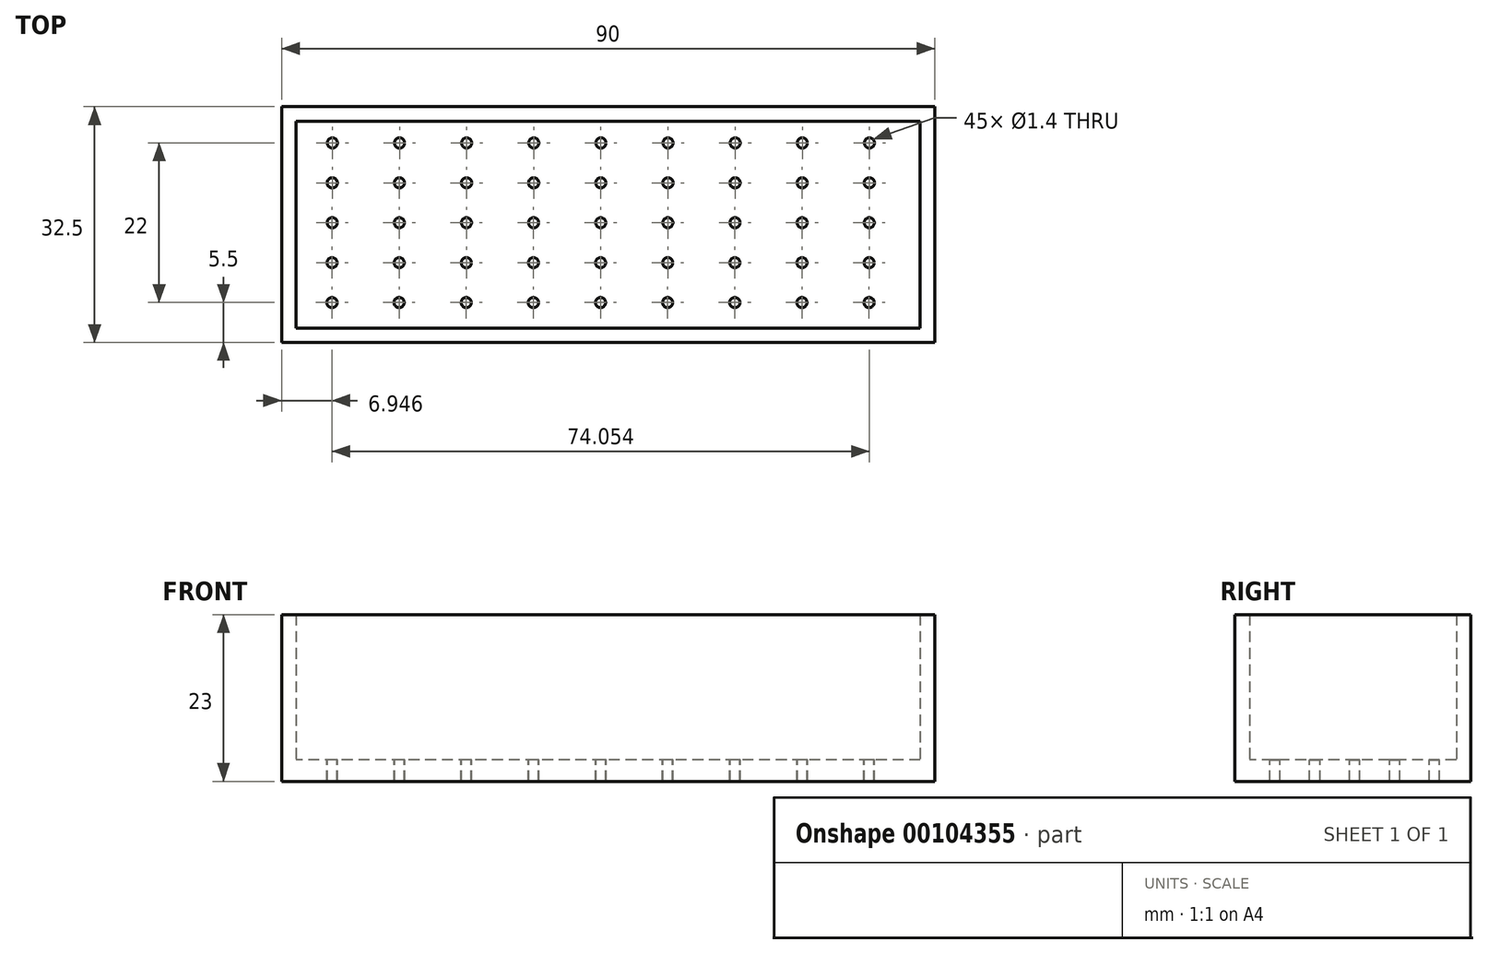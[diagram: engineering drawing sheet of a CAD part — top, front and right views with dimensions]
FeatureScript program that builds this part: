
annotation { "Feature Type Name" : "Feature", "Feature Type Description" : "" }
export const myFeature = defineFeature(function(context is Context, id is Id, definition is map)
    precondition{}
    {
        {
            var Q0;
            Q0=qCreatedBy(makeId("Top.planeOp"),FACE);
            var sketch = newSketch(context, id + "F0", { "sketchPlane" : qUnion([Q0])});
            skLineSegment(sketch, "E0.bottom", {"start": v(-45, 16.25) * mm, "end": v(45, 16.25) * mm});
            skLineSegment(sketch, "E0.top", {"start": v(-45, -16.25) * mm, "end": v(45, -16.25) * mm});
            skLineSegment(sketch, "E0.left", {"start": v(-45, 16.25) * mm, "end": v(-45, -16.25) * mm});
            skLineSegment(sketch, "E0.right", {"start": v(45, 16.25) * mm, "end": v(45, -16.25) * mm});
            skPoint(sketch, "E0.middle", {"position": v(0, 0) * mm});
            skSolve(sketch);
        }
        {
            var Q0;
            Q0 = qSketchRegion(id + "F0", true);
            extrude(context, id + "F1", {"entities" : qUnion([Q0]), "depth" : 3 * mm});
        }
        {
            var Q0;
            Q0=makeQuery(id+"F1.opExtrude","CAP_FACE",FACE,{"disambiguationData":[OSD([sQuery(id+"F0.wireOp",EDGE,"E0.bottom"),sQuery(id+"F0.wireOp",EDGE,"E0.top"),sQuery(id+"F0.wireOp",EDGE,"E0.left"),sQuery(id+"F0.wireOp",EDGE,"E0.right")])],"isStart":false});
            var sketch = newSketch(context, id + "F2", { "sketchPlane" : qUnion([Q0])});
            skLineSegment(sketch, "E1", {"start": v(-45, 16.25) * mm, "end": v(-45, -16.25) * mm});
            skLineSegment(sketch, "E2", {"start": v(-45, -16.25) * mm, "end": v(45, -16.25) * mm});
            skLineSegment(sketch, "E3", {"start": v(45, -16.25) * mm, "end": v(45, 16.25) * mm});
            skLineSegment(sketch, "E4", {"start": v(45, 16.25) * mm, "end": v(-45, 16.25) * mm});
            skLineSegment(sketch, "E5", {"start": v(-43, 14.25) * mm, "end": v(-43, -14.25) * mm});
            skLineSegment(sketch, "E6", {"start": v(-43, -14.25) * mm, "end": v(43, -14.25) * mm});
            skLineSegment(sketch, "E7", {"start": v(43, -14.25) * mm, "end": v(43, 14.25) * mm});
            skLineSegment(sketch, "E8", {"start": v(43, 14.25) * mm, "end": v(-43, 14.25) * mm});
            skSolve(sketch);
        }
        {
            var Q0;
            Q0=makeQuery(id+"F2.imprint","IMPRINT",FACE,{"disambiguationData":[TD([[makeQuery(id+"F2.imprint","IMPRINT",EDGE,{"derivedFrom":sQuery(id+"F2.wireOp",EDGE,"E1")}),1.0]])]});
            extrude(context, id + "F3", {"entities" : qUnion([Q0]), "operationType" : NewBodyOperationType.ADD, "depth" : 20 * mm});
        }
        {
            var Q0;
            Q0=makeQuery(id+"F1.opExtrude","CAP_FACE",FACE,{"disambiguationData":[OSD([sQuery(id+"F0.wireOp",EDGE,"E0.bottom"),sQuery(id+"F0.wireOp",EDGE,"E0.top"),sQuery(id+"F0.wireOp",EDGE,"E0.left"),sQuery(id+"F0.wireOp",EDGE,"E0.right")])],"isStart":false});
            var sketch = newSketch(context, id + "F4", { "sketchPlane" : qUnion([Q0])});
            skCircle(sketch, "E9", {"center": v(-38, 11.25) * mm, "radius": 0.7 * mm});
            skCircle(sketch, "E10.1.0.0", {"center": v(-28.75, 11.25) * mm, "radius": 0.7 * mm});
            skCircle(sketch, "E10.2.0.0", {"center": v(-19.5, 11.25) * mm, "radius": 0.7 * mm});
            skCircle(sketch, "E10.3.0.0", {"center": v(-10.25, 11.25) * mm, "radius": 0.7 * mm});
            skCircle(sketch, "E10.4.0.0", {"center": v(-1, 11.25) * mm, "radius": 0.7 * mm});
            skCircle(sketch, "E10.5.0.0", {"center": v(8.25, 11.25) * mm, "radius": 0.7 * mm});
            skCircle(sketch, "E10.6.0.0", {"center": v(17.5, 11.25) * mm, "radius": 0.7 * mm});
            skCircle(sketch, "E10.7.0.0", {"center": v(26.75, 11.25) * mm, "radius": 0.7 * mm});
            skCircle(sketch, "E10.8.0.0", {"center": v(36, 11.25) * mm, "radius": 0.7 * mm});
            skLineSegment(sketch, "E10.direction1", {"start": v(-38, 11.25) * mm, "end": v(-28.75, 11.25) * mm, "construction": true});
            skCircle(sketch, "E11.1.0.0", {"center": v(-38.01, 5.75) * mm, "radius": 0.7 * mm});
            skCircle(sketch, "E11.2.0.0", {"center": v(-38.03, 0.25) * mm, "radius": 0.7 * mm});
            skCircle(sketch, "E11.3.0.0", {"center": v(-38.04, -5.25) * mm, "radius": 0.7 * mm});
            skCircle(sketch, "E11.4.0.0", {"center": v(-38.05, -10.75) * mm, "radius": 0.7 * mm});
            skLineSegment(sketch, "E11.direction1", {"start": v(-38, 11.25) * mm, "end": v(-38.01, 5.75) * mm, "construction": true});
            skCircle(sketch, "E12.1.0.0", {"center": v(-28.76, 5.75) * mm, "radius": 0.7 * mm});
            skCircle(sketch, "E12.1.0.1", {"center": v(-28.78, 0.25) * mm, "radius": 0.7 * mm});
            skCircle(sketch, "E12.1.0.2", {"center": v(-28.8, -5.25) * mm, "radius": 0.7 * mm});
            skCircle(sketch, "E12.1.0.3", {"center": v(-28.8, -10.75) * mm, "radius": 0.7 * mm});
            skCircle(sketch, "E12.2.0.0", {"center": v(-19.51, 5.75) * mm, "radius": 0.7 * mm});
            skCircle(sketch, "E12.2.0.1", {"center": v(-19.53, 0.25) * mm, "radius": 0.7 * mm});
            skCircle(sketch, "E12.2.0.2", {"center": v(-19.54, -5.25) * mm, "radius": 0.7 * mm});
            skCircle(sketch, "E12.2.0.3", {"center": v(-19.55, -10.75) * mm, "radius": 0.7 * mm});
            skCircle(sketch, "E12.3.0.0", {"center": v(-10.26, 5.75) * mm, "radius": 0.7 * mm});
            skCircle(sketch, "E12.3.0.1", {"center": v(-10.28, 0.25) * mm, "radius": 0.7 * mm});
            skCircle(sketch, "E12.3.0.2", {"center": v(-10.3, -5.25) * mm, "radius": 0.7 * mm});
            skCircle(sketch, "E12.3.0.3", {"center": v(-10.3, -10.75) * mm, "radius": 0.7 * mm});
            skCircle(sketch, "E12.4.0.0", {"center": v(-1.01, 5.75) * mm, "radius": 0.7 * mm});
            skCircle(sketch, "E12.4.0.1", {"center": v(-1.03, 0.25) * mm, "radius": 0.7 * mm});
            skCircle(sketch, "E12.4.0.2", {"center": v(-1.04, -5.25) * mm, "radius": 0.7 * mm});
            skCircle(sketch, "E12.4.0.3", {"center": v(-1.05, -10.75) * mm, "radius": 0.7 * mm});
            skCircle(sketch, "E12.5.0.0", {"center": v(8.24, 5.75) * mm, "radius": 0.7 * mm});
            skCircle(sketch, "E12.5.0.1", {"center": v(8.22, 0.25) * mm, "radius": 0.7 * mm});
            skCircle(sketch, "E12.5.0.2", {"center": v(8.2, -5.25) * mm, "radius": 0.7 * mm});
            skCircle(sketch, "E12.5.0.3", {"center": v(8.2, -10.75) * mm, "radius": 0.7 * mm});
            skCircle(sketch, "E12.6.0.0", {"center": v(17.49, 5.75) * mm, "radius": 0.7 * mm});
            skCircle(sketch, "E12.6.0.1", {"center": v(17.47, 0.25) * mm, "radius": 0.7 * mm});
            skCircle(sketch, "E12.6.0.2", {"center": v(17.46, -5.25) * mm, "radius": 0.7 * mm});
            skCircle(sketch, "E12.6.0.3", {"center": v(17.45, -10.75) * mm, "radius": 0.7 * mm});
            skCircle(sketch, "E12.7.0.0", {"center": v(26.74, 5.75) * mm, "radius": 0.7 * mm});
            skCircle(sketch, "E12.7.0.1", {"center": v(26.72, 0.25) * mm, "radius": 0.7 * mm});
            skCircle(sketch, "E12.7.0.2", {"center": v(26.7, -5.25) * mm, "radius": 0.7 * mm});
            skCircle(sketch, "E12.7.0.3", {"center": v(26.7, -10.75) * mm, "radius": 0.7 * mm});
            skCircle(sketch, "E12.8.0.0", {"center": v(35.99, 5.75) * mm, "radius": 0.7 * mm});
            skCircle(sketch, "E12.8.0.1", {"center": v(35.97, 0.25) * mm, "radius": 0.7 * mm});
            skCircle(sketch, "E12.8.0.2", {"center": v(35.96, -5.25) * mm, "radius": 0.7 * mm});
            skCircle(sketch, "E12.8.0.3", {"center": v(35.95, -10.75) * mm, "radius": 0.7 * mm});
            skLineSegment(sketch, "E12.direction1", {"start": v(-38.05, -10.75) * mm, "end": v(-28.8, -10.75) * mm, "construction": true});
            skSolve(sketch);
        }
        {
            var Q0;
            Q0 = qSketchRegion(id + "F4", true);
            extrude(context, id + "F5", {"entities" : qUnion([Q0]), "operationType" : NewBodyOperationType.REMOVE, "endBound" : BoundingType.THROUGH_ALL, "oppositeDirection" : true, "depth" : 25 * mm});
        }
    });
